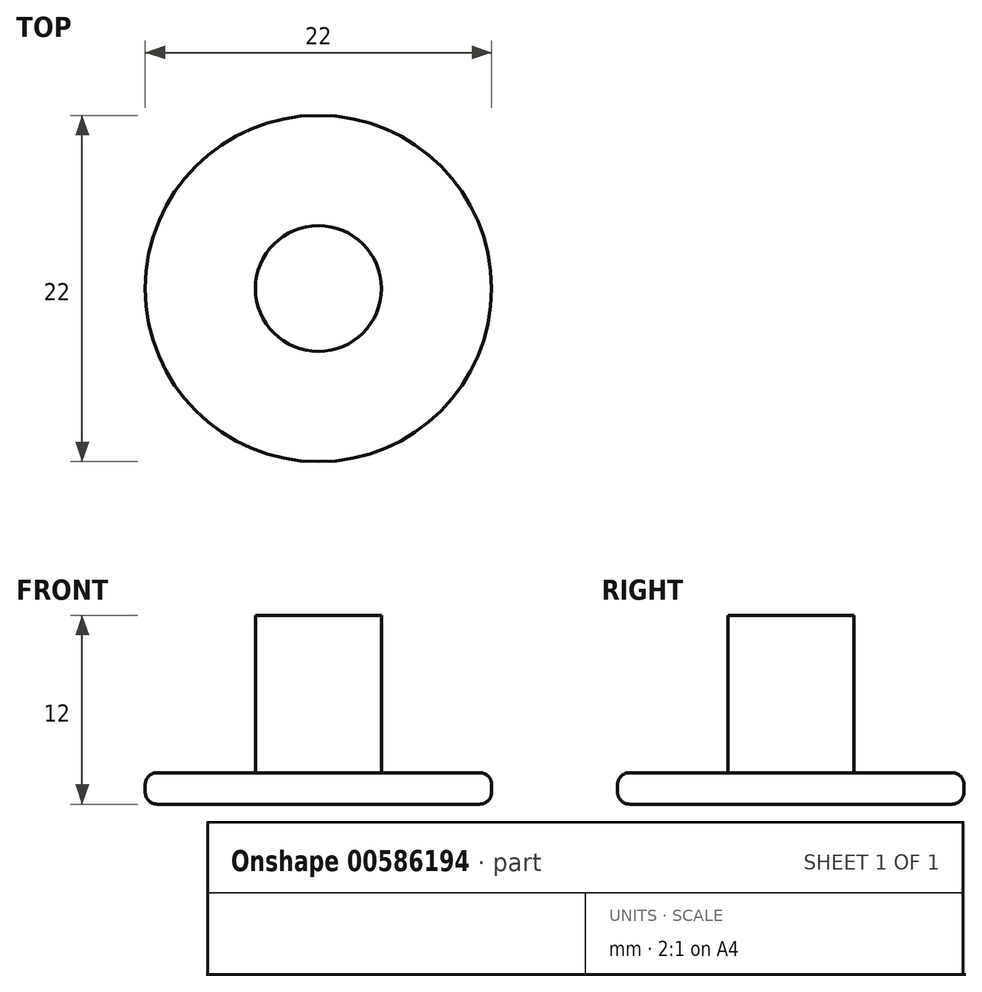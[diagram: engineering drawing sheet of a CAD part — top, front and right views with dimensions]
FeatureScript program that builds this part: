
annotation { "Feature Type Name" : "Feature", "Feature Type Description" : "" }
export const myFeature = defineFeature(function(context is Context, id is Id, definition is map)
    precondition{}
    {
        {
            var Q0;
            Q0=qCreatedBy(makeId("Top.planeOp"),FACE);
            var sketch = newSketch(context, id + "F0", { "sketchPlane" : qUnion([Q0])});
            skCircle(sketch, "E0", {"center": v(0, 0) * mm, "radius": 11 * mm});
            skSolve(sketch);
        }
        {
            var Q0;
            Q0=qSketchRegion(id+"F0",true);
            extrude(context, id + "F1", {"entities" : qUnion([Q0]), "depth" : 2 * mm, "offsetDistance" : 25.4 * mm});
        }
        {
            var Q0;
            Q0=qCreatedBy(makeId("Top.planeOp"),FACE);
            var sketch = newSketch(context, id + "F2", { "sketchPlane" : qUnion([Q0])});
            skCircle(sketch, "E1", {"center": v(0, 0) * mm, "radius": 4 * mm});
            skSolve(sketch);
        }
        {
            var Q0;
            Q0=makeQuery(id+"F2.imprint","IMPRINT",FACE,{"disambiguationData":[TD([[makeQuery(id+"F2.imprint","IMPRINT",EDGE,{"derivedFrom":sQuery(id+"F2.wireOp",EDGE,"E1")}),1.0]])]});
            extrude(context, id + "F3", {"entities" : qUnion([Q0]), "operationType" : NewBodyOperationType.ADD, "depth" : 12 * mm, "offsetDistance" : 25.4 * mm});
        }
        {
            var Q0;
            Q0=makeQuery(id+"F1.opExtrude","CAP_EDGE",EDGE,{"disambiguationData":[OSD([sQuery(id+"F0.wireOp",EDGE,"E0")])],"isStart":false});
            var Q1;
            Q1=makeQuery(id+"F1.opExtrude","SWEPT_FACE",FACE,{"disambiguationData":[OSD([sQuery(id+"F0.wireOp",EDGE,"E0")])]});
            fillet(context, id + "F4", {"entities" : qUnion([Q0, Q1]), "radius" : 0.76 * mm, "tangentPropagation" : true, "allowEdgeOverflow" : false});
        }
    });
